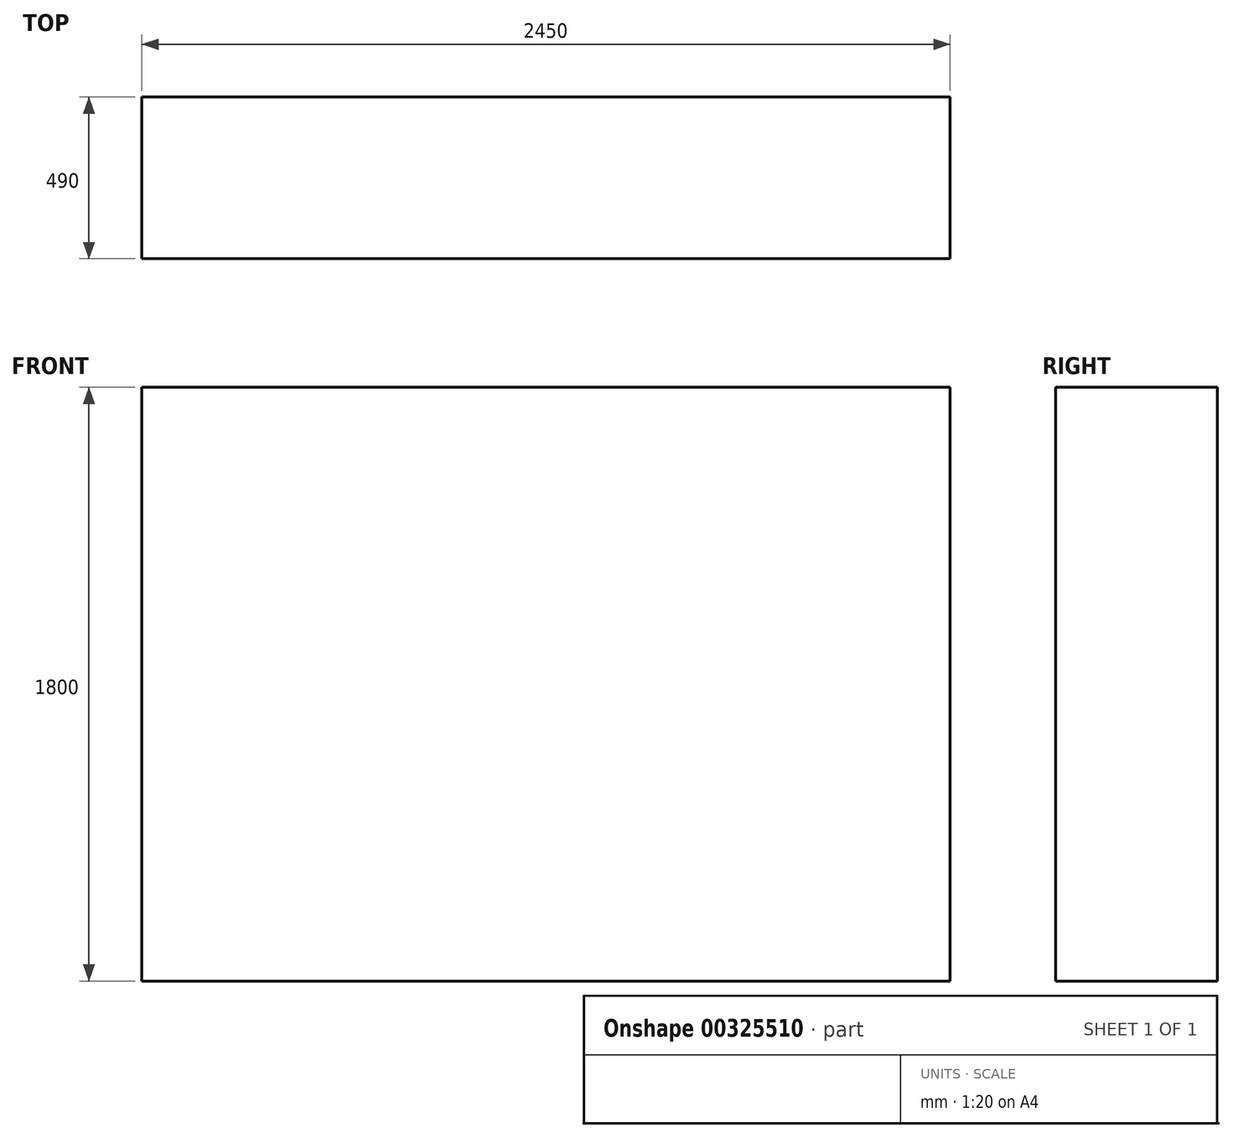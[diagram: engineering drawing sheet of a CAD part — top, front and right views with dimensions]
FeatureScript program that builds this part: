
annotation { "Feature Type Name" : "Feature", "Feature Type Description" : "" }
export const myFeature = defineFeature(function(context is Context, id is Id, definition is map)
    precondition{}
    {
        {
            var Q0;
            Q0=qCreatedBy(makeId("Top.planeOp"),FACE);
            var sketch = newSketch(context, id + "F0", { "sketchPlane" : qUnion([Q0])});
            skLineSegment(sketch, "E0.bottom", {"start": v(1225, -245) * mm, "end": v(-1225, -245) * mm});
            skLineSegment(sketch, "E0.top", {"start": v(1225, 245) * mm, "end": v(-1225, 245) * mm});
            skLineSegment(sketch, "E0.left", {"start": v(1225, -245) * mm, "end": v(1225, 245) * mm});
            skLineSegment(sketch, "E0.right", {"start": v(-1225, -245) * mm, "end": v(-1225, 245) * mm});
            skPoint(sketch, "E0.middle", {"position": v(0, 0) * mm});
            skSolve(sketch);
        }
        {
            var Q0;
            Q0 = qSketchRegion(id + "F0", true);
            extrude(context, id + "F1", {"entities" : qUnion([Q0]), "depth" : 1800 * mm});
        }
    });
